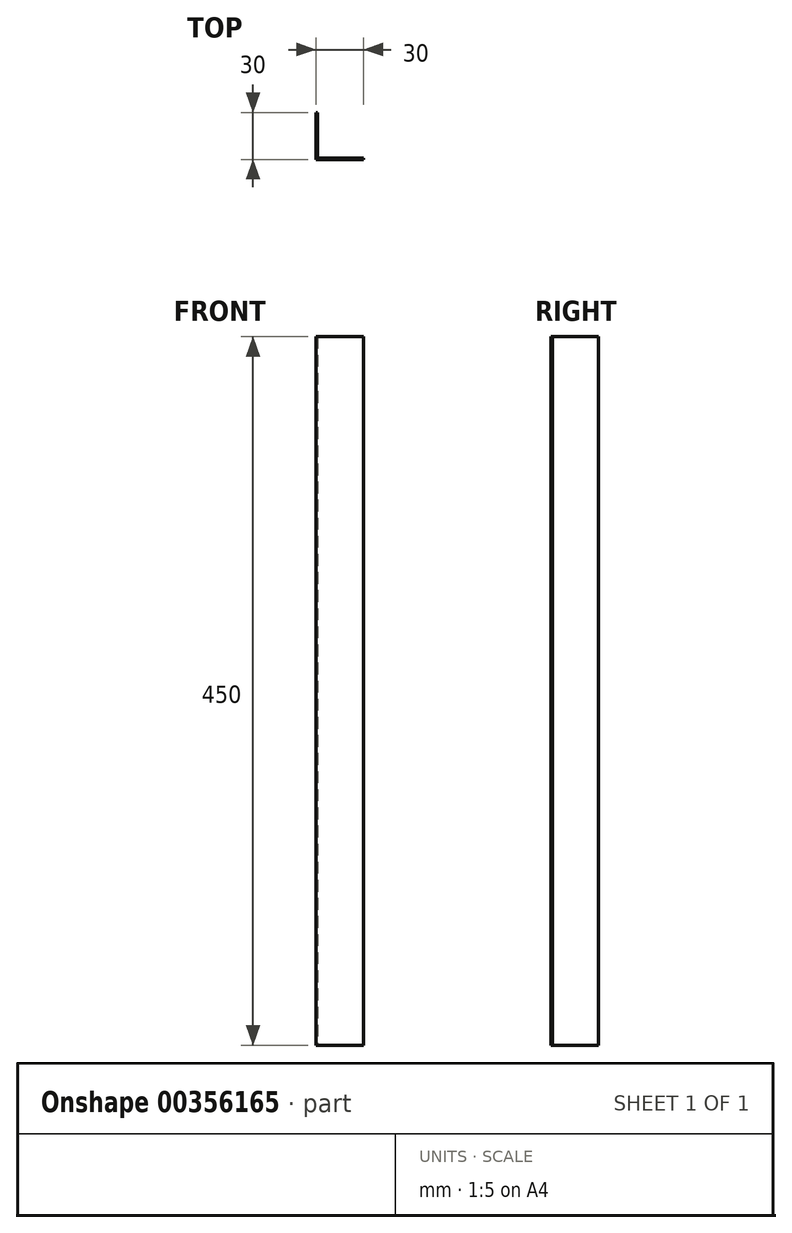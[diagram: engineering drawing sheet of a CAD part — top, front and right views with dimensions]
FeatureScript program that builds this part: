
annotation { "Feature Type Name" : "Feature", "Feature Type Description" : "" }
export const myFeature = defineFeature(function(context is Context, id is Id, definition is map)
    precondition{}
    {
        {
            var Q0;
            Q0=qCreatedBy(makeId("Top.planeOp"),FACE);
            var sketch = newSketch(context, id + "F0", { "sketchPlane" : qUnion([Q0])});
            skLineSegment(sketch, "E0.bottom", {"start": v(15, -15) * mm, "end": v(-15, -15) * mm});
            skLineSegment(sketch, "E0.top", {"start": v(-14.1, 15) * mm, "end": v(-15, 15) * mm});
            skLineSegment(sketch, "E0.left", {"start": v(15, -15) * mm, "end": v(15, -14.1) * mm});
            skLineSegment(sketch, "E0.right", {"start": v(-15, -15) * mm, "end": v(-15, 15) * mm});
            skPoint(sketch, "E0.middle", {"position": v(0, 0) * mm});
            skLineSegment(sketch, "E1", {"start": v(-14.1, 15) * mm, "end": v(-14.1, -14.1) * mm});
            skLineSegment(sketch, "E2", {"start": v(-14.1, -14.1) * mm, "end": v(15, -14.1) * mm});
            skSolve(sketch);
        }
        {
            var Q0;
            Q0 = qSketchRegion(id + "F0", true);
            extrude(context, id + "F1", {"entities" : qUnion([Q0]), "endBound" : BoundingType.SYMMETRIC, "depth" : 450 * mm});
        }
    });
